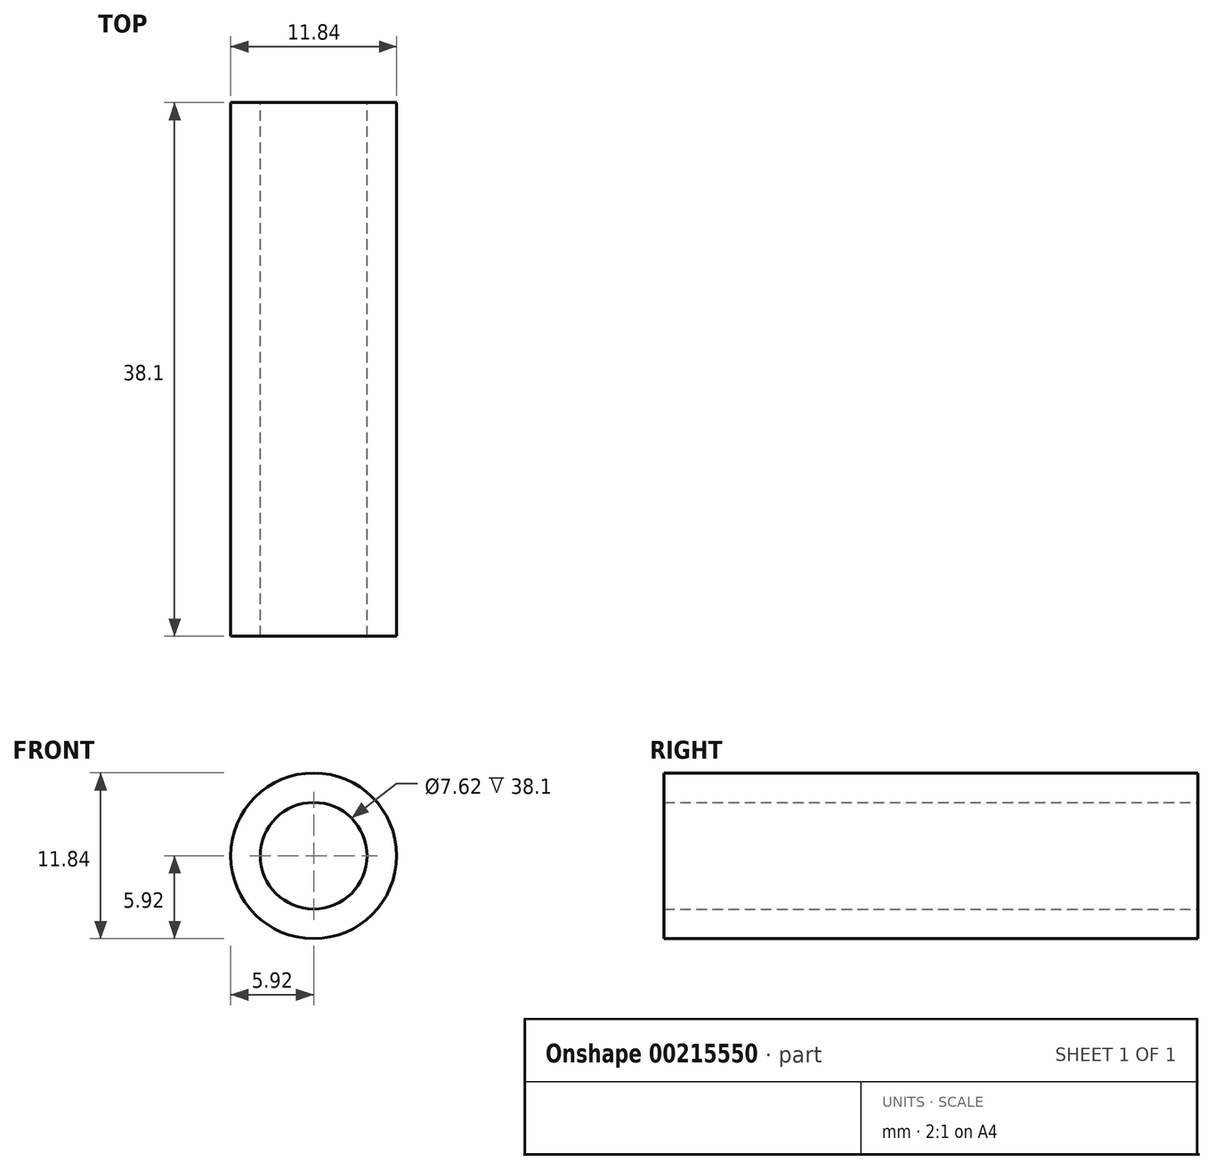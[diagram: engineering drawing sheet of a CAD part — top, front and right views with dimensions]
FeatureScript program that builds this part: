
annotation { "Feature Type Name" : "Feature", "Feature Type Description" : "" }
export const myFeature = defineFeature(function(context is Context, id is Id, definition is map)
    precondition{}
    {
        {
            var Q0;
            Q0=qCreatedBy(makeId("Front.planeOp"),FACE);
            var sketch = newSketch(context, id + "F0", { "sketchPlane" : qUnion([Q0])});
            skCircle(sketch, "E0", {"center": v(0, 0) * mm, "radius": 3.81 * mm});
            skCircle(sketch, "E1", {"center": v(0, 0) * mm, "radius": 5.92 * mm});
            skSolve(sketch);
        }
        {
            var Q0;
            Q0 = qSketchRegion(id + "F0", true);
            extrude(context, id + "F1", {"entities" : qUnion([Q0]), "depth" : 38.1 * mm});
        }
    });
